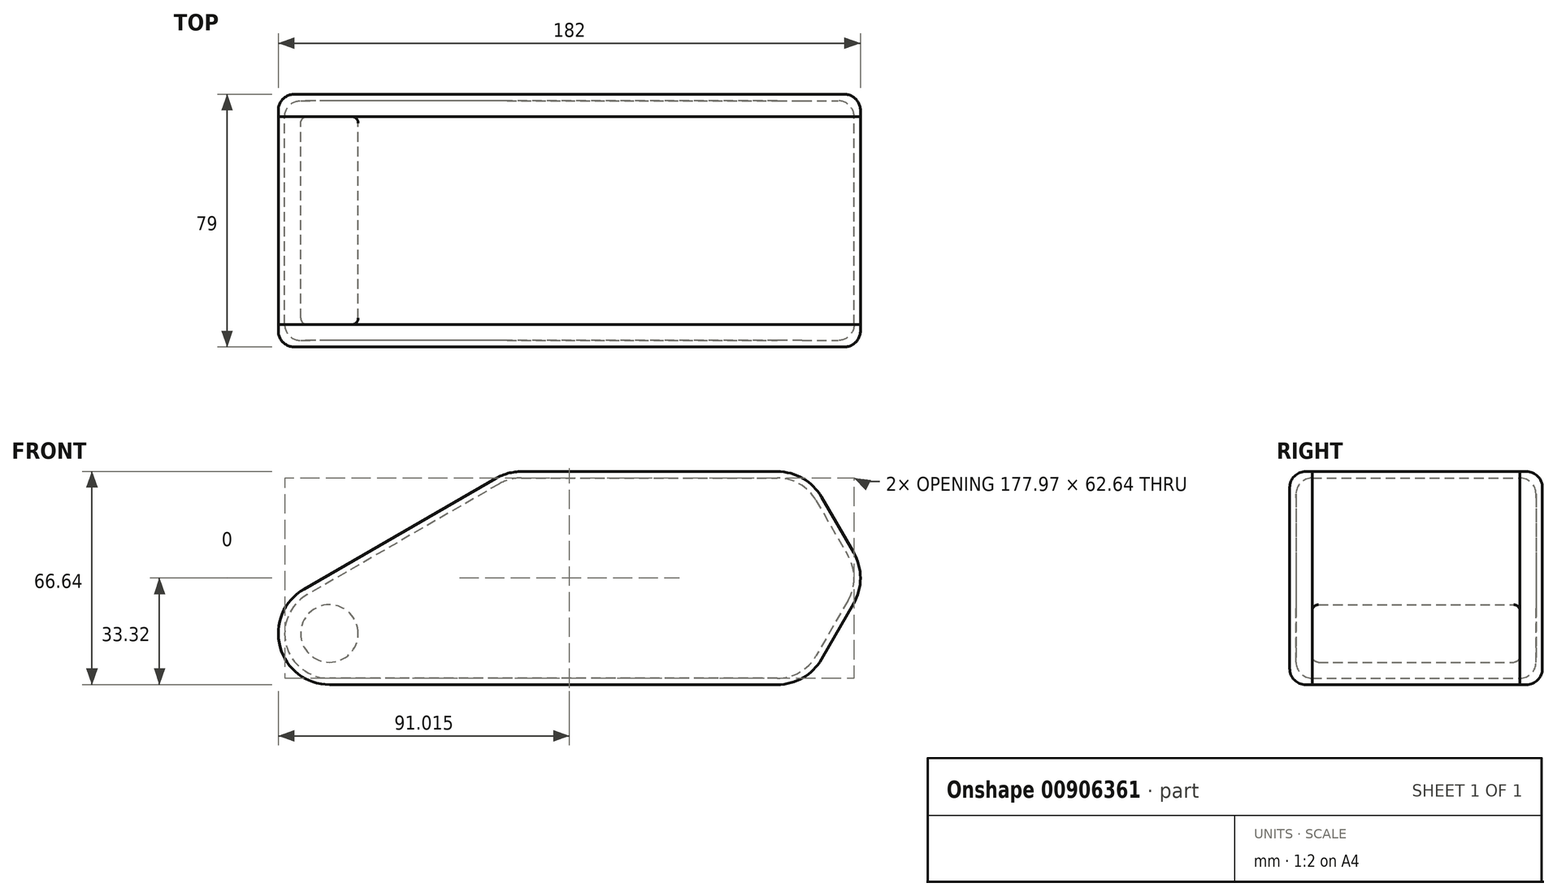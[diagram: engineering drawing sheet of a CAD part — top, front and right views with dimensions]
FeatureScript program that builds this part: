
annotation { "Feature Type Name" : "Feature", "Feature Type Description" : "" }
export const myFeature = defineFeature(function(context is Context, id is Id, definition is map)
    precondition{}
    {
        {
            var Q0;
            Q0=qCreatedBy(makeId("Front.planeOp"),FACE);
            var sketch = newSketch(context, id + "F0", { "sketchPlane" : qUnion([Q0])});
            skCircle(sketch, "E0", {"center": v(0, 0) * mm, "radius": 9 * mm});
            skCircle(sketch, "E1.1.0.0", {"center": v(20, 0) * mm, "radius": 9 * mm});
            skCircle(sketch, "E1.1.1.0", {"center": v(30, 17.32) * mm, "radius": 9 * mm});
            skCircle(sketch, "E1.2.0.0", {"center": v(40, 0) * mm, "radius": 9 * mm});
            skCircle(sketch, "E1.2.1.0", {"center": v(50, 17.32) * mm, "radius": 9 * mm});
            skCircle(sketch, "E1.2.2.0", {"center": v(60, 34.64) * mm, "radius": 9 * mm});
            skCircle(sketch, "E1.3.0.0", {"center": v(60, 0) * mm, "radius": 9 * mm});
            skCircle(sketch, "E1.3.1.0", {"center": v(70, 17.32) * mm, "radius": 9 * mm});
            skCircle(sketch, "E1.3.2.0", {"center": v(80, 34.64) * mm, "radius": 9 * mm});
            skCircle(sketch, "E1.4.0.0", {"center": v(80, 0) * mm, "radius": 9 * mm});
            skCircle(sketch, "E1.4.1.0", {"center": v(90, 17.32) * mm, "radius": 9 * mm});
            skCircle(sketch, "E1.4.2.0", {"center": v(100, 34.64) * mm, "radius": 9 * mm});
            skCircle(sketch, "E1.5.0.0", {"center": v(100, 0) * mm, "radius": 9 * mm});
            skCircle(sketch, "E1.5.1.0", {"center": v(110, 17.32) * mm, "radius": 9 * mm});
            skCircle(sketch, "E1.5.2.0", {"center": v(120, 34.64) * mm, "radius": 9 * mm});
            skCircle(sketch, "E1.6.0.0", {"center": v(120, 0) * mm, "radius": 9 * mm});
            skCircle(sketch, "E1.6.1.0", {"center": v(130, 17.32) * mm, "radius": 9 * mm});
            skCircle(sketch, "E1.6.2.0", {"center": v(140, 34.64) * mm, "radius": 9 * mm});
            skCircle(sketch, "E1.7.0.0", {"center": v(140, 0) * mm, "radius": 9 * mm});
            skCircle(sketch, "E1.7.1.0", {"center": v(150, 17.32) * mm, "radius": 9 * mm});
            skLineSegment(sketch, "E1.direction1", {"start": v(0, 0) * mm, "end": v(20, 0) * mm, "construction": true});
            skLineSegment(sketch, "E1.direction2", {"start": v(0, 0) * mm, "end": v(10.55, 18.27) * mm, "construction": true});
            skSolve(sketch);
        }
        {
            var Q0;
            Q0=makeQuery(id+"F0.imprint","IMPRINT",FACE,{"disambiguationData":[TD([[makeQuery(id+"F0.imprint","IMPRINT",EDGE,{"derivedFrom":sQuery(id+"F0.wireOp",EDGE,"E0")}),1.0]])]});
            extrude(context, id + "F1", {"entities" : qUnion([Q0]), "depth" : 65 * mm, "offsetDistance" : 25 * mm});
        }
        {
            var Q0;
            Q0=makeQuery(id+"F1.opExtrude","CAP_EDGE",EDGE,{"disambiguationData":[OSD([sQuery(id+"F0.wireOp",EDGE,"E0")])],"isStart":true});
            var Q1;
            Q1=makeQuery(id+"F1.opExtrude","CAP_EDGE",EDGE,{"disambiguationData":[OSD([sQuery(id+"F0.wireOp",EDGE,"E0")])],"isStart":false});
            fillet(context, id + "F2", {"entities" : qUnion([Q0, Q1]), "radius" : 2 * mm, "tangentPropagation" : true, "allowEdgeOverflow" : false});
        }
        {
            var Q0;
            Q0=qCreatedBy(makeId("Front.planeOp"),FACE);
            var sketch = newSketch(context, id + "F3", { "sketchPlane" : qUnion([Q0])});
            skArc(sketch, "E2.0", {"start": v(60, 43.64) * mm, "mid": v(57.67, 43.33) * mm, "end": v(55.5, 42.44) * mm});
            skArc(sketch, "E3.0", {"start": v(147.8, 39.14) * mm, "mid": v(144.5, 42.44) * mm, "end": v(140, 43.64) * mm});
            skArc(sketch, "E4.0", {"start": v(157.8, 12.82) * mm, "mid": v(159, 17.32) * mm, "end": v(157.8, 21.82) * mm});
            skArc(sketch, "E5.0", {"start": v(140, -9) * mm, "mid": v(144.5, -7.8) * mm, "end": v(147.8, -4.5) * mm});
            skArc(sketch, "E6.0", {"start": v(-4.5, 7.8) * mm, "mid": v(-8.7, -2.33) * mm, "end": v(0, -9) * mm});
            skLineSegment(sketch, "E7", {"start": v(60, 43.64) * mm, "end": v(140, 43.64) * mm});
            skLineSegment(sketch, "E8", {"start": v(147.8, 39.14) * mm, "end": v(157.8, 21.82) * mm});
            skLineSegment(sketch, "E9", {"start": v(157.8, 12.82) * mm, "end": v(147.8, -4.5) * mm});
            skLineSegment(sketch, "E10", {"start": v(140, -9) * mm, "end": v(0, -9) * mm});
            skLineSegment(sketch, "E11", {"start": v(55.5, 42.44) * mm, "end": v(25.5, 25.11) * mm});
            skLineSegment(sketch, "E12", {"start": v(25.5, 25.11) * mm, "end": v(-4.5, 7.8) * mm});
            skLineSegment(sketch, "E13.0", {"start": v(162.12, 10.32) * mm, "end": v(152.12, -7) * mm});
            skArc(sketch, "E13.1", {"start": v(162.12, 10.32) * mm, "mid": v(164, 17.32) * mm, "end": v(162.12, 24.32) * mm});
            skLineSegment(sketch, "E13.2", {"start": v(152.12, 41.64) * mm, "end": v(162.12, 24.32) * mm});
            skArc(sketch, "E13.3", {"start": v(152.12, 41.64) * mm, "mid": v(147, 46.77) * mm, "end": v(140, 48.64) * mm});
            skLineSegment(sketch, "E13.4", {"start": v(60, 48.64) * mm, "end": v(140, 48.64) * mm});
            skArc(sketch, "E13.5", {"start": v(140, -14) * mm, "mid": v(147, -12.12) * mm, "end": v(152.12, -7) * mm});
            skLineSegment(sketch, "E13.6", {"start": v(140, -14) * mm, "end": v(0, -14) * mm});
            skArc(sketch, "E13.7", {"start": v(-7, 12.12) * mm, "mid": v(-13.52, -3.62) * mm, "end": v(0, -14) * mm});
            skLineSegment(sketch, "E13.8", {"start": v(23, 29.44) * mm, "end": v(-7, 12.12) * mm});
            skLineSegment(sketch, "E13.9", {"start": v(53, 46.77) * mm, "end": v(23, 29.44) * mm});
            skArc(sketch, "E13.10", {"start": v(60, 48.64) * mm, "mid": v(56.38, 48.16) * mm, "end": v(53, 46.77) * mm});
            skLineSegment(sketch, "E14.0", {"start": v(140, -16) * mm, "end": v(0, -16) * mm});
            skArc(sketch, "E14.1", {"start": v(-8, 13.86) * mm, "mid": v(-15.45, -4.14) * mm, "end": v(0, -16) * mm});
            skLineSegment(sketch, "E14.2", {"start": v(22, 31.18) * mm, "end": v(-8, 13.86) * mm});
            skLineSegment(sketch, "E14.3", {"start": v(52, 48.5) * mm, "end": v(22, 31.18) * mm});
            skArc(sketch, "E14.4", {"start": v(60, 50.64) * mm, "mid": v(55.86, 50.1) * mm, "end": v(52, 48.5) * mm});
            skArc(sketch, "E14.5", {"start": v(140, -16) * mm, "mid": v(148, -13.86) * mm, "end": v(153.86, -8) * mm});
            skLineSegment(sketch, "E14.6", {"start": v(163.86, 9.32) * mm, "end": v(153.86, -8) * mm});
            skArc(sketch, "E14.7", {"start": v(163.86, 9.32) * mm, "mid": v(166, 17.32) * mm, "end": v(163.86, 25.32) * mm});
            skLineSegment(sketch, "E14.8", {"start": v(153.86, 42.64) * mm, "end": v(163.86, 25.32) * mm});
            skArc(sketch, "E14.9", {"start": v(153.86, 42.64) * mm, "mid": v(148, 48.5) * mm, "end": v(140, 50.64) * mm});
            skLineSegment(sketch, "E14.10", {"start": v(60, 50.64) * mm, "end": v(140, 50.64) * mm});
            skSolve(sketch);
        }
        {
            var Q0;
            Q0=makeQuery(id+"F3.imprint","IMPRINT",FACE,{"disambiguationData":[TD([[makeQuery(id+"F3.imprint","IMPRINT",EDGE,{"derivedFrom":sQuery(id+"F3.wireOp",EDGE,"E13.0")}),1.0]])]});
            extrude(context, id + "F4", {"entities" : qUnion([Q0]), "depth" : 65 * mm, "offsetDistance" : 25 * mm});
        }
        {
            var Q0;
            Q0=makeQuery(id+"F4.opExtrude","CAP_FACE",FACE,{"disambiguationData":[OSD([sQuery(id+"F3.wireOp",EDGE,"E13.0"),sQuery(id+"F3.wireOp",EDGE,"E13.1"),sQuery(id+"F3.wireOp",EDGE,"E13.2"),sQuery(id+"F3.wireOp",EDGE,"E13.3"),sQuery(id+"F3.wireOp",EDGE,"E13.4"),sQuery(id+"F3.wireOp",EDGE,"E13.5"),sQuery(id+"F3.wireOp",EDGE,"E13.6"),sQuery(id+"F3.wireOp",EDGE,"E13.7"),sQuery(id+"F3.wireOp",EDGE,"E13.8"),sQuery(id+"F3.wireOp",EDGE,"E13.9"),sQuery(id+"F3.wireOp",EDGE,"E13.10"),sQuery(id+"F3.wireOp",EDGE,"E14.0"),sQuery(id+"F3.wireOp",EDGE,"E14.1"),sQuery(id+"F3.wireOp",EDGE,"E14.2"),sQuery(id+"F3.wireOp",EDGE,"E14.3"),sQuery(id+"F3.wireOp",EDGE,"E14.4"),sQuery(id+"F3.wireOp",EDGE,"E14.5"),sQuery(id+"F3.wireOp",EDGE,"E14.6"),sQuery(id+"F3.wireOp",EDGE,"E14.7"),sQuery(id+"F3.wireOp",EDGE,"E14.8"),sQuery(id+"F3.wireOp",EDGE,"E14.9"),sQuery(id+"F3.wireOp",EDGE,"E14.10")])],"isStart":true});
            var sketch = newSketch(context, id + "F5", { "sketchPlane" : qUnion([Q0])});
            skLineSegment(sketch, "E15.0", {"start": v(-153.86, 42.64) * mm, "end": v(-163.86, 25.32) * mm});
            skArc(sketch, "E16.0", {"start": v(-153.86, 42.64) * mm, "mid": v(-148, 48.5) * mm, "end": v(-140, 50.64) * mm});
            skLineSegment(sketch, "E17.0", {"start": v(-152.12, 41.64) * mm, "end": v(-162.12, 24.32) * mm});
            skArc(sketch, "E18.0", {"start": v(-152.12, 41.64) * mm, "mid": v(-147, 46.77) * mm, "end": v(-140, 48.64) * mm});
            skLineSegment(sketch, "E19.0", {"start": v(-60, 48.64) * mm, "end": v(-140, 48.64) * mm});
            skLineSegment(sketch, "E20.0", {"start": v(-60, 50.64) * mm, "end": v(-140, 50.64) * mm});
            skArc(sketch, "E21.0", {"start": v(-162.12, 10.32) * mm, "mid": v(-164, 17.32) * mm, "end": v(-162.12, 24.32) * mm});
            skArc(sketch, "E22.0", {"start": v(-163.86, 9.32) * mm, "mid": v(-166, 17.32) * mm, "end": v(-163.86, 25.32) * mm});
            skLineSegment(sketch, "E23.0", {"start": v(-163.86, 9.32) * mm, "end": v(-153.86, -8) * mm});
            skLineSegment(sketch, "E24.0", {"start": v(-162.12, 10.32) * mm, "end": v(-152.12, -7) * mm});
            skArc(sketch, "E25.0", {"start": v(-140, -14) * mm, "mid": v(-147, -12.12) * mm, "end": v(-152.12, -7) * mm});
            skArc(sketch, "E26.0", {"start": v(-140, -16) * mm, "mid": v(-148, -13.86) * mm, "end": v(-153.86, -8) * mm});
            skLineSegment(sketch, "E27.0", {"start": v(-140, -16) * mm, "end": v(0, -16) * mm});
            skLineSegment(sketch, "E28.0", {"start": v(-140, -14) * mm, "end": v(0, -14) * mm});
            skArc(sketch, "E29.0", {"start": v(-60, 48.64) * mm, "mid": v(-56.38, 48.16) * mm, "end": v(-53, 46.77) * mm});
            skArc(sketch, "E30.0", {"start": v(-60, 50.64) * mm, "mid": v(-55.86, 50.1) * mm, "end": v(-52, 48.5) * mm});
            skLineSegment(sketch, "E31.0", {"start": v(-52, 48.5) * mm, "end": v(8, 13.86) * mm});
            skLineSegment(sketch, "E32.0", {"start": v(-53, 46.77) * mm, "end": v(7, 12.12) * mm});
            skArc(sketch, "E33.0", {"start": v(8, 13.86) * mm, "mid": v(15.45, -4.14) * mm, "end": v(0, -16) * mm});
            skArc(sketch, "E34.0", {"start": v(7, 12.12) * mm, "mid": v(13.52, -3.62) * mm, "end": v(0, -14) * mm});
            skSolve(sketch);
        }
        {
            var Q0;
            Q0=makeQuery(id+"F5.imprint","IMPRINT",FACE,{"disambiguationData":[TD([[makeQuery(id+"F5.imprint","IMPRINT",EDGE,{"derivedFrom":sQuery(id+"F5.wireOp",EDGE,"E15.0")}),1.0]])]});
            extrude(context, id + "F6", {"entities" : qUnion([Q0]), "depth" : 5 * mm, "offsetDistance" : 25 * mm});
        }
        {
            var Q0;
            Q0=makeQuery(id+"F6.opExtrude","CAP_FACE",FACE,{"disambiguationData":[OSD([sQuery(id+"F5.wireOp",EDGE,"E15.0"),sQuery(id+"F5.wireOp",EDGE,"E16.0"),sQuery(id+"F5.wireOp",EDGE,"E17.0"),sQuery(id+"F5.wireOp",EDGE,"E18.0"),sQuery(id+"F5.wireOp",EDGE,"E19.0"),sQuery(id+"F5.wireOp",EDGE,"E20.0"),sQuery(id+"F5.wireOp",EDGE,"E21.0"),sQuery(id+"F5.wireOp",EDGE,"E22.0"),sQuery(id+"F5.wireOp",EDGE,"E23.0"),sQuery(id+"F5.wireOp",EDGE,"E24.0"),sQuery(id+"F5.wireOp",EDGE,"E25.0"),sQuery(id+"F5.wireOp",EDGE,"E26.0"),sQuery(id+"F5.wireOp",EDGE,"E27.0"),sQuery(id+"F5.wireOp",EDGE,"E28.0"),sQuery(id+"F5.wireOp",EDGE,"E29.0"),sQuery(id+"F5.wireOp",EDGE,"E30.0"),sQuery(id+"F5.wireOp",EDGE,"E31.0"),sQuery(id+"F5.wireOp",EDGE,"E32.0"),sQuery(id+"F5.wireOp",EDGE,"E33.0"),sQuery(id+"F5.wireOp",EDGE,"E34.0")])],"isStart":false});
            var sketch = newSketch(context, id + "F7", { "sketchPlane" : qUnion([Q0])});
            skArc(sketch, "E35.0.0", {"start": v(-52, 48.5) * mm, "mid": v(-55.86, 50.1) * mm, "end": v(-60, 50.64) * mm});
            skLineSegment(sketch, "E35.0.1", {"start": v(-60, 50.64) * mm, "end": v(-140, 50.64) * mm});
            skArc(sketch, "E35.0.2", {"start": v(-140, 50.64) * mm, "mid": v(-148, 48.5) * mm, "end": v(-153.86, 42.64) * mm});
            skLineSegment(sketch, "E35.0.3", {"start": v(-153.86, 42.64) * mm, "end": v(-163.86, 25.32) * mm});
            skArc(sketch, "E35.0.4", {"start": v(-163.86, 25.32) * mm, "mid": v(-166, 17.32) * mm, "end": v(-163.86, 9.32) * mm});
            skLineSegment(sketch, "E35.0.5", {"start": v(-163.86, 9.32) * mm, "end": v(-153.86, -8) * mm});
            skArc(sketch, "E35.0.6", {"start": v(-153.86, -8) * mm, "mid": v(-148, -13.86) * mm, "end": v(-140, -16) * mm});
            skLineSegment(sketch, "E35.0.7", {"start": v(-140, -16) * mm, "end": v(0, -16) * mm});
            skArc(sketch, "E35.0.8", {"start": v(0, -16) * mm, "mid": v(15.45, -4.14) * mm, "end": v(8, 13.86) * mm});
            skLineSegment(sketch, "E35.0.9", {"start": v(8, 13.86) * mm, "end": v(-52, 48.5) * mm});
            skSolve(sketch);
        }
        {
            var Q0;
            Q0=makeQuery(id+"F7.imprint","IMPRINT",FACE,{"disambiguationData":[TD([[makeQuery(id+"F7.imprint","IMPRINT",EDGE,{"derivedFrom":makeQuery(id+"F6.opExtrude","CAP_EDGE",EDGE,{"disambiguationData":[OSD([sQuery(id+"F5.wireOp",EDGE,"E17.0")])],"isStart":false})}),1.0]])]});
            var Q1;
            Q1=makeQuery(id+"F7.imprint","IMPRINT",FACE,{"disambiguationData":[TD([[makeQuery(id+"F7.imprint","IMPRINT",EDGE,{"derivedFrom":sQuery(id+"F7.wireOp",EDGE,"E35.0.0")}),-1.0]])]});
            extrude(context, id + "F8", {"entities" : qUnion([Q0, Q1]), "operationType" : NewBodyOperationType.ADD, "depth" : 2 * mm, "offsetDistance" : 25 * mm});
        }
        {
            var Q0;
            Q0=makeQuery(id+"F8.opExtrude","CAP_FACE",FACE,{"disambiguationData":[OSD([sQuery(id+"F7.wireOp",EDGE,"E35.0.0"),sQuery(id+"F7.wireOp",EDGE,"E35.0.1"),sQuery(id+"F7.wireOp",EDGE,"E35.0.2"),sQuery(id+"F7.wireOp",EDGE,"E35.0.3"),sQuery(id+"F7.wireOp",EDGE,"E35.0.4"),sQuery(id+"F7.wireOp",EDGE,"E35.0.5"),sQuery(id+"F7.wireOp",EDGE,"E35.0.6"),sQuery(id+"F7.wireOp",EDGE,"E35.0.7"),sQuery(id+"F7.wireOp",EDGE,"E35.0.8"),sQuery(id+"F7.wireOp",EDGE,"E35.0.9")])],"isStart":false});
            fillet(context, id + "F9", {"entities" : qUnion([Q0]), "radius" : 5 * mm, "tangentPropagation" : true, "allowEdgeOverflow" : false});
        }
        {
            var Q0;
            Q0=makeQuery(id+"F8.opExtrude","CAP_FACE",FACE,{"disambiguationData":[OSD([sQuery(id+"F7.wireOp",EDGE,"E35.0.0"),sQuery(id+"F7.wireOp",EDGE,"E35.0.1"),sQuery(id+"F7.wireOp",EDGE,"E35.0.2"),sQuery(id+"F7.wireOp",EDGE,"E35.0.3"),sQuery(id+"F7.wireOp",EDGE,"E35.0.4"),sQuery(id+"F7.wireOp",EDGE,"E35.0.5"),sQuery(id+"F7.wireOp",EDGE,"E35.0.6"),sQuery(id+"F7.wireOp",EDGE,"E35.0.7"),sQuery(id+"F7.wireOp",EDGE,"E35.0.8"),sQuery(id+"F7.wireOp",EDGE,"E35.0.9")])],"isStart":true});
            fillet(context, id + "F10", {"entities" : qUnion([Q0]), "radius" : 5 * mm, "tangentPropagation" : true, "allowEdgeOverflow" : false});
        }
        {
            var Q0;
            Q0=qCreatedBy(makeId("Front.planeOp"),FACE);
            cPlane(context, id + "F11", {"entities" : qUnion([Q0]), "cplaneType" : CPlaneType.OFFSET, "offset" : 32.5 * mm, "width" : 150 * mm, "height" : 150 * mm});
        }
        {
            var Q0;
            Q0=makeQuery(id+"F6.opExtrude","SWEPT_BODY",BODY,{"disambiguationData":[OSD([sQuery(id+"F5.wireOp",EDGE,"E15.0"),sQuery(id+"F5.wireOp",EDGE,"E16.0"),sQuery(id+"F5.wireOp",EDGE,"E17.0"),sQuery(id+"F5.wireOp",EDGE,"E18.0"),sQuery(id+"F5.wireOp",EDGE,"E19.0"),sQuery(id+"F5.wireOp",EDGE,"E20.0"),sQuery(id+"F5.wireOp",EDGE,"E21.0"),sQuery(id+"F5.wireOp",EDGE,"E22.0"),sQuery(id+"F5.wireOp",EDGE,"E23.0"),sQuery(id+"F5.wireOp",EDGE,"E24.0"),sQuery(id+"F5.wireOp",EDGE,"E25.0"),sQuery(id+"F5.wireOp",EDGE,"E26.0"),sQuery(id+"F5.wireOp",EDGE,"E27.0"),sQuery(id+"F5.wireOp",EDGE,"E28.0"),sQuery(id+"F5.wireOp",EDGE,"E29.0"),sQuery(id+"F5.wireOp",EDGE,"E30.0"),sQuery(id+"F5.wireOp",EDGE,"E31.0"),sQuery(id+"F5.wireOp",EDGE,"E32.0"),sQuery(id+"F5.wireOp",EDGE,"E33.0"),sQuery(id+"F5.wireOp",EDGE,"E34.0")])]});
            var Q1;
            Q1=qCreatedBy(id+"F11.planeOp",FACE);
            mirror(context, id + "F12", {"entities" : qUnion([Q0]), "mirrorPlane" : qUnion([Q1])});
        }
    });
